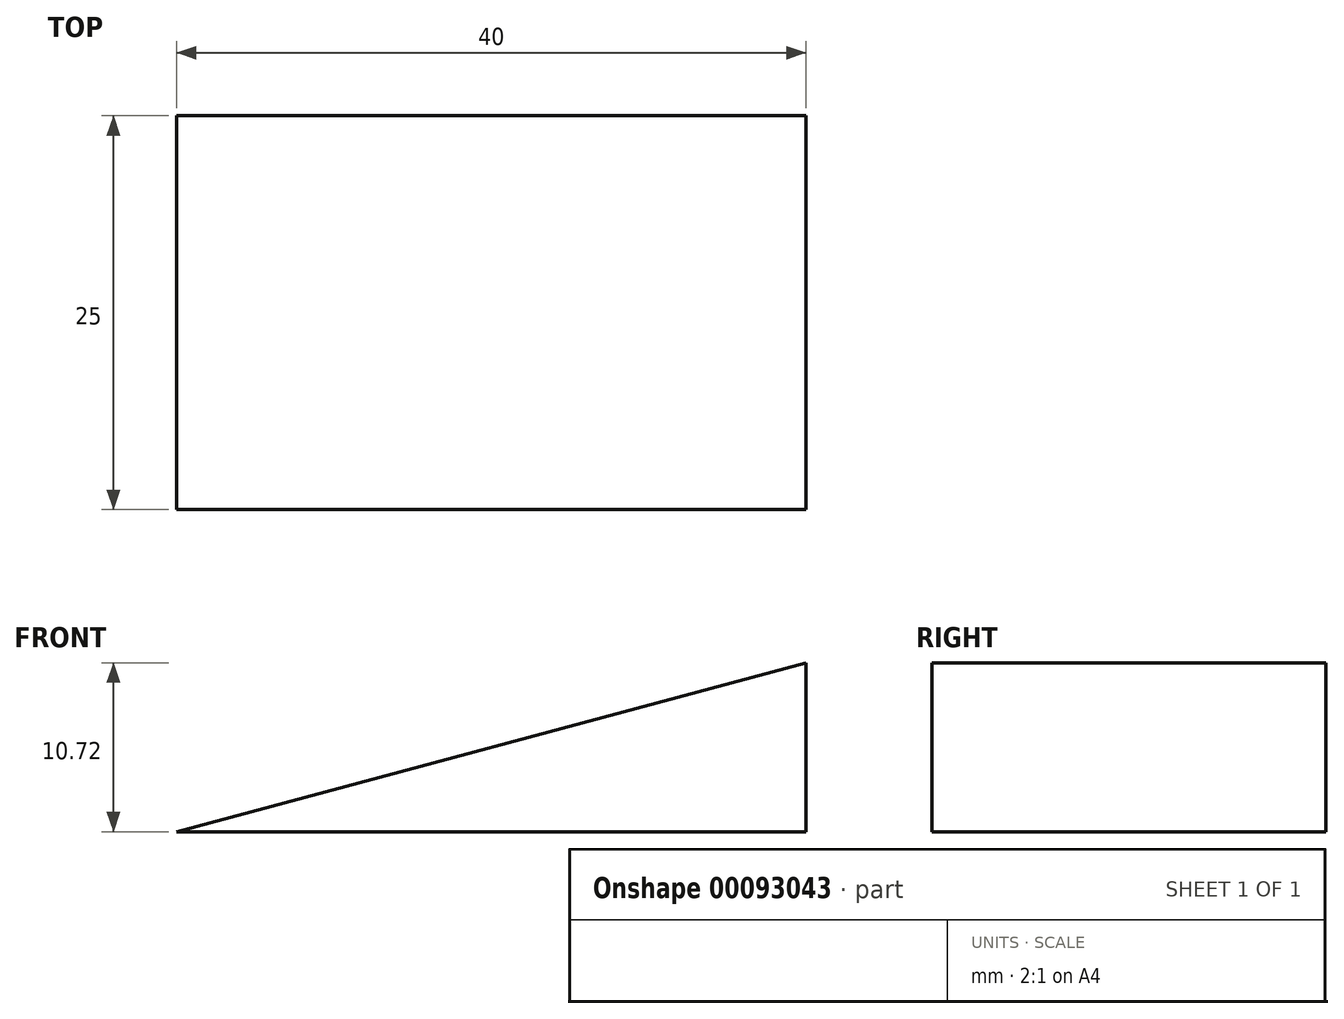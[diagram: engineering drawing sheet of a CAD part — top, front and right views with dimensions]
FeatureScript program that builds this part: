
annotation { "Feature Type Name" : "Feature", "Feature Type Description" : "" }
export const myFeature = defineFeature(function(context is Context, id is Id, definition is map)
    precondition{}
    {
        {
            var Q0;
            Q0=qCreatedBy(makeId("Front.planeOp"),FACE);
            var sketch = newSketch(context, id + "F0", { "sketchPlane" : qUnion([Q0])});
            skLineSegment(sketch, "E0", {"start": v(-20, 0) * mm, "end": v(20, 0) * mm});
            skLineSegment(sketch, "E1", {"start": v(20, 0) * mm, "end": v(20, 10.72) * mm});
            skLineSegment(sketch, "E2", {"start": v(20, 10.72) * mm, "end": v(-20, 0) * mm});
            skSolve(sketch);
        }
        {
            var Q0;
            Q0=makeQuery(id+"F0.imprint","IMPRINT",FACE,{"disambiguationData":[TD([[makeQuery(id+"F0.imprint","IMPRINT",EDGE,{"derivedFrom":sQuery(id+"F0.wireOp",EDGE,"E0")}),1.0]])]});
            extrude(context, id + "F1", {"entities" : qUnion([Q0]), "depth" : 25 * mm});
        }
    });
